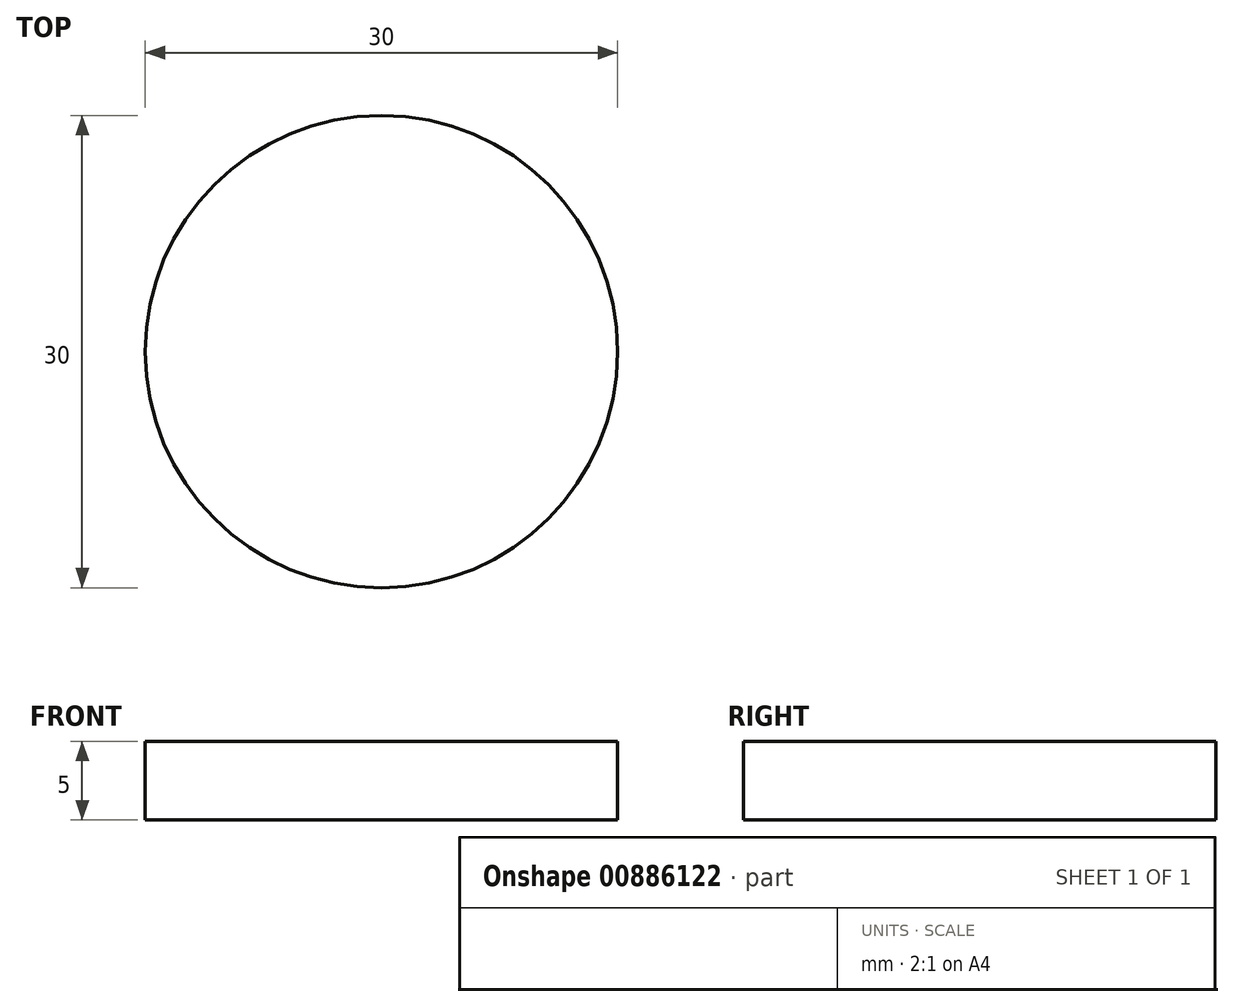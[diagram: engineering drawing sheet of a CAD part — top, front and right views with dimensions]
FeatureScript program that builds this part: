
annotation { "Feature Type Name" : "Feature", "Feature Type Description" : "" }
export const myFeature = defineFeature(function(context is Context, id is Id, definition is map)
    precondition{}
    {
        {
            var Q0;
            Q0=qCreatedBy(makeId("Top.planeOp"),FACE);
            var sketch = newSketch(context, id + "F0", { "sketchPlane" : qUnion([Q0])});
            skCircle(sketch, "E0", {"center": v(0, 0) * mm, "radius": 15 * mm});
            skSolve(sketch);
        }
        {
            var Q0;
            Q0=makeQuery(id+"F0.imprint","IMPRINT",FACE,{"disambiguationData":[TD([[makeQuery(id+"F0.imprint","IMPRINT",EDGE,{"derivedFrom":sQuery(id+"F0.wireOp",EDGE,"E0")}),1.0]])]});
            extrude(context, id + "F1", {"entities" : qUnion([Q0]), "depth" : 5 * mm, "offsetDistance" : 25 * mm});
        }
    });
